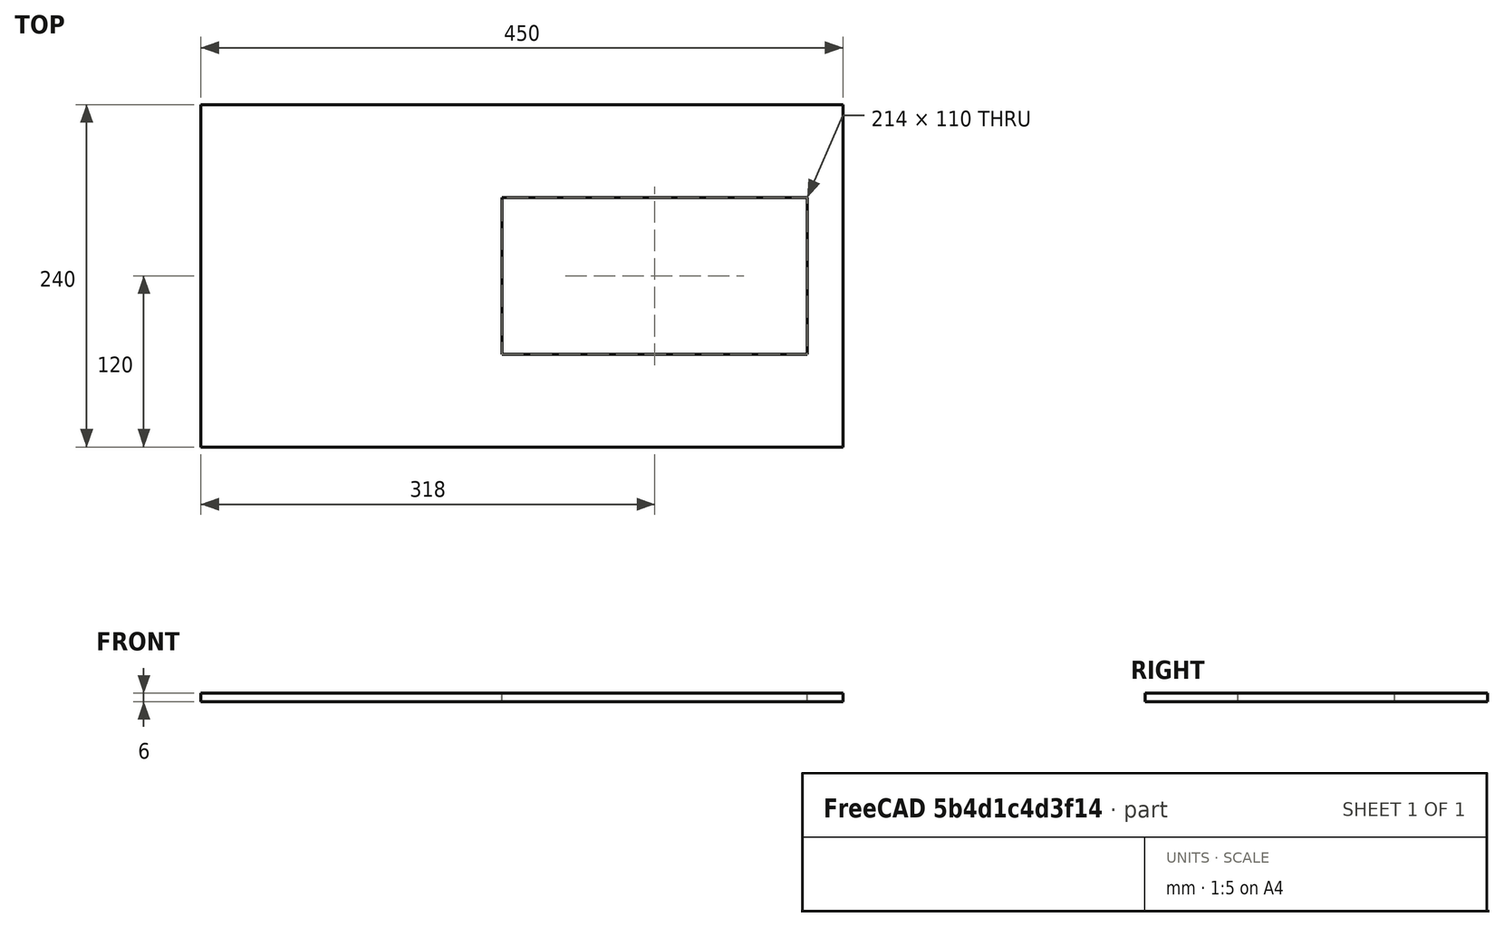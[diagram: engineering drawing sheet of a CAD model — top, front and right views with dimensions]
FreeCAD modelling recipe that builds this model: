
FCSTD DOCUMENT  (FreeCAD 0.18R4 (GitTag))
Label: cubierta_husillos
License: All rights reserved
LicenseURL: http://en.wikipedia.org/wiki/All_rights_reserved
objects: Sketcher::SketchObject×1, PartDesign::Pad×1, PartDesign::Body×1
note: 4 computed .brp shape members not serialized (recipe doc carries the construction recipe); baked Part::Feature solids carry a one-line shape summary decoded from their .brp

FEATURE [Sketcher::SketchObject] Sketch
  MapMode = 5
  Support = -> [XY_Plane]
  sketch-geometry (8):
    g0: LineSegment StartX=0 StartY=0 StartZ=0 EndX=450 EndY=0 EndZ=0
    g1: LineSegment StartX=450 StartY=0 StartZ=0 EndX=450 EndY=240 EndZ=0
    g2: LineSegment StartX=450 StartY=240 StartZ=0 EndX=0 EndY=240 EndZ=0
    g3: LineSegment StartX=0 StartY=240 StartZ=0 EndX=0 EndY=0 EndZ=0
    g4: LineSegment StartX=211 StartY=175 StartZ=0 EndX=425 EndY=175 EndZ=0
    g5: LineSegment StartX=425 StartY=175 StartZ=0 EndX=425 EndY=65 EndZ=0
    g6: LineSegment StartX=425 StartY=65 StartZ=0 EndX=211 EndY=65 EndZ=0
    g7: LineSegment StartX=211 StartY=65 StartZ=0 EndX=211 EndY=175 EndZ=0
  constraints (23):
    c: Coincident(g0,g1)
    c: Coincident(g1,g2)
    c: Coincident(g2,g3)
    c: Coincident(g3,g0)
    c: Horizontal(g0)
    c: Horizontal(g2)
    c: Vertical(g1)
    c: Vertical(g3)
    c: DistanceX(g0,g0) = 450
    c: Coincident(g0,g-1)
    c: DistanceY(g3,g3) = 240
    c: Coincident(g4,g5)
    c: Coincident(g5,g6)
    c: Coincident(g6,g7)
    c: Coincident(g7,g4)
    c: Horizontal(g4)
    c: Horizontal(g6)
    c: Vertical(g5)
    c: Vertical(g7)
    c: Distance(g4,g3) = 211
    c: Distance(g4,g1) = 25
    c: Distance(g6,g0) = 65
    c: Distance(g4,g2) = 65
FEATURE [PartDesign::Pad] Pad
  Length = 6
  Length2 = 100
  Profile = -> Sketch
  Type = 0
FEATURE [PartDesign::Body] Body
  Group = -> [Sketch,Pad]
  Origin = -> Origin
  Tip = -> Pad
